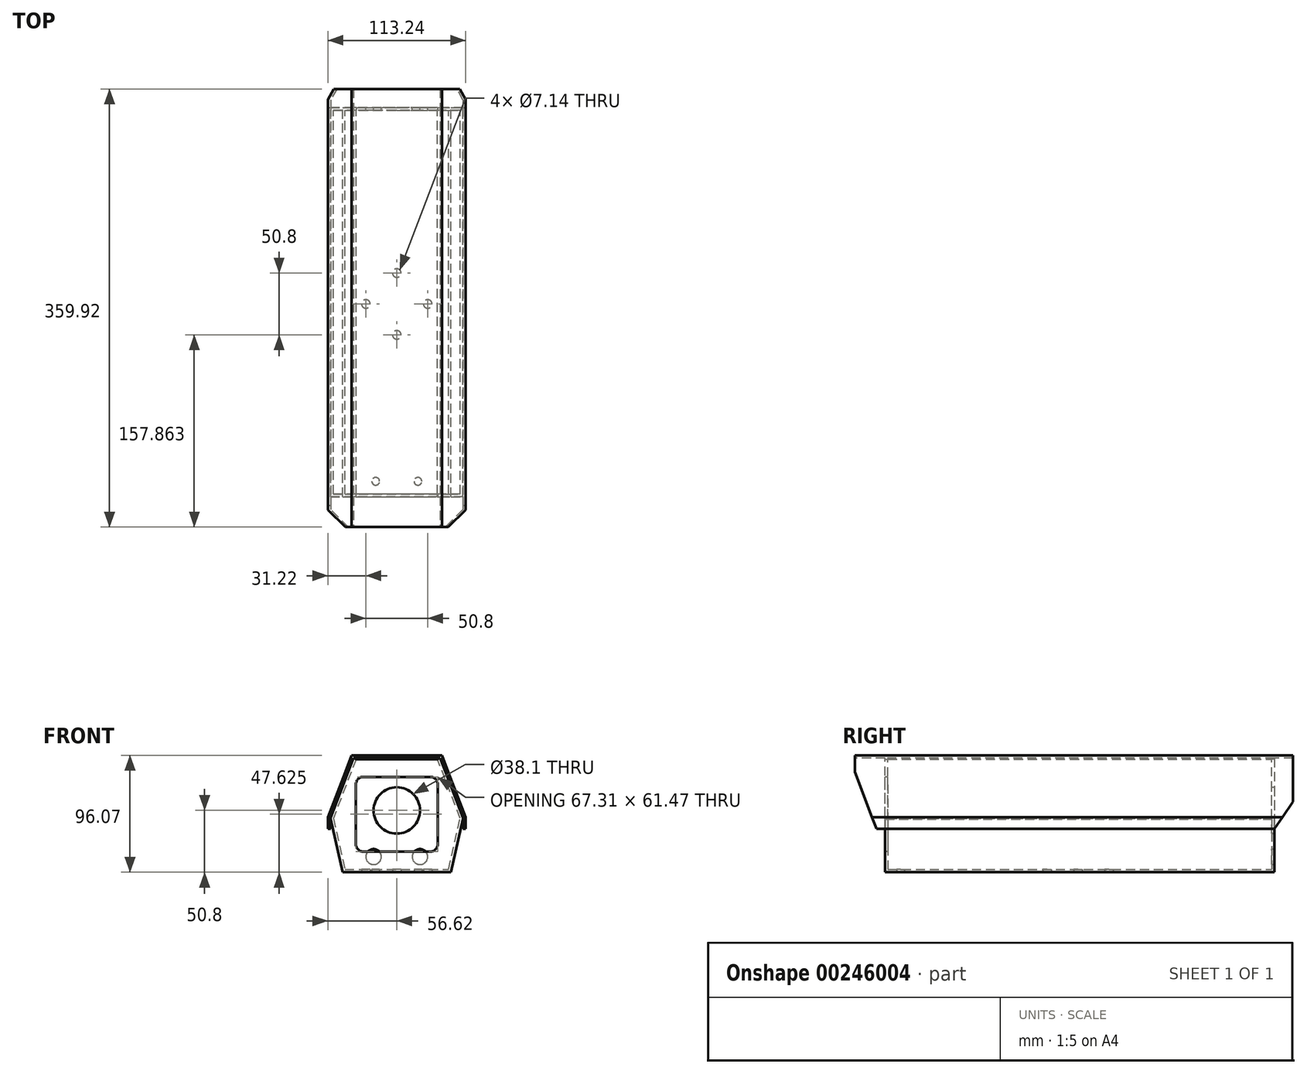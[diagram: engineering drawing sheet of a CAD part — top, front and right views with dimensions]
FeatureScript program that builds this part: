
annotation { "Feature Type Name" : "Feature", "Feature Type Description" : "" }
export const myFeature = defineFeature(function(context is Context, id is Id, definition is map)
    precondition{}
    {
        {
            var Q0;
            Q0=qCreatedBy(makeId("Front.planeOp"),FACE);
            var sketch = newSketch(context, id + "F0", { "sketchPlane" : qUnion([Q0])});
            skLineSegment(sketch, "E0", {"start": v(-44.45, 0) * mm, "end": v(44.45, 0) * mm});
            skLineSegment(sketch, "E1", {"start": v(44.45, 0) * mm, "end": v(54.48, 44.45) * mm});
            skLineSegment(sketch, "E2", {"start": v(54.48, 44.45) * mm, "end": v(34.92, 95.25) * mm});
            skLineSegment(sketch, "E3", {"start": v(34.92, 95.25) * mm, "end": v(-34.92, 95.25) * mm});
            skLineSegment(sketch, "E4", {"start": v(-34.92, 95.25) * mm, "end": v(-54.48, 44.45) * mm});
            skLineSegment(sketch, "E5", {"start": v(-54.48, 44.45) * mm, "end": v(-44.45, 0) * mm});
            skLineSegment(sketch, "E6", {"start": v(0, -51.88) * mm, "end": v(0, 117.86) * mm, "construction": true});
            skSolve(sketch);
        }
        {
            var Q0;
            Q0=makeQuery(id+"F0.imprint","IMPRINT",FACE,{"disambiguationData":[TD([[makeQuery(id+"F0.imprint","IMPRINT",EDGE,{"derivedFrom":sQuery(id+"F0.wireOp",EDGE,"E0")}),1.0]])]});
            extrude(context, id + "F1", {"entities" : qUnion([Q0]), "depth" : 319.8 * mm});
        }
        {
            var Q0;
            Q0=makeQuery(id+"F1.opExtrude","CAP_FACE",FACE,{"disambiguationData":[OSD([sQuery(id+"F0.wireOp",EDGE,"E0"),sQuery(id+"F0.wireOp",EDGE,"E1"),sQuery(id+"F0.wireOp",EDGE,"E2"),sQuery(id+"F0.wireOp",EDGE,"E3"),sQuery(id+"F0.wireOp",EDGE,"E4"),sQuery(id+"F0.wireOp",EDGE,"E5")])],"isStart":false});
            shell(context, id + "F2", {"entities" : qUnion([Q0]), "thickness" : 2.3 * mm});
        }
        {
            var Q0;
            Q0=makeQuery(id+"F1.opExtrude","CAP_FACE",FACE,{"disambiguationData":[OSD([sQuery(id+"F0.wireOp",EDGE,"E0"),sQuery(id+"F0.wireOp",EDGE,"E1"),sQuery(id+"F0.wireOp",EDGE,"E2"),sQuery(id+"F0.wireOp",EDGE,"E3"),sQuery(id+"F0.wireOp",EDGE,"E4"),sQuery(id+"F0.wireOp",EDGE,"E5")])],"isStart":true});
            var sketch = newSketch(context, id + "F3", { "sketchPlane" : qUnion([Q0])});
            skCircle(sketch, "E7", {"center": v(-19.05, 12.7) * mm, "radius": 6.35 * mm});
            skCircle(sketch, "E8", {"center": v(19.05, 12.7) * mm, "radius": 6.35 * mm});
            skLineSegment(sketch, "E9", {"start": v(0, 105.87) * mm, "end": v(0, -20.53) * mm, "construction": true});
            skSolve(sketch);
        }
        {
            var Q0;
            Q0=makeQuery(id+"F3.imprint","IMPRINT",FACE,{"disambiguationData":[TD([[makeQuery(id+"F3.imprint","IMPRINT",EDGE,{"derivedFrom":sQuery(id+"F3.wireOp",EDGE,"E7")}),1.0]])]});
            var Q1;
            Q1=makeQuery(id+"F3.imprint","IMPRINT",FACE,{"disambiguationData":[TD([[makeQuery(id+"F3.imprint","IMPRINT",EDGE,{"derivedFrom":sQuery(id+"F3.wireOp",EDGE,"E8")}),1.0]])]});
            extrude(context, id + "F4", {"entities" : qUnion([Q0, Q1]), "operationType" : NewBodyOperationType.REMOVE, "endBound" : BoundingType.UP_TO_NEXT, "oppositeDirection" : true, "depth" : 25.4 * mm});
        }
        {
            var Q0;
            Q0=makeQuery(id+"F1.opExtrude","CAP_FACE",FACE,{"disambiguationData":[OSD([sQuery(id+"F0.wireOp",EDGE,"E0"),sQuery(id+"F0.wireOp",EDGE,"E1"),sQuery(id+"F0.wireOp",EDGE,"E2"),sQuery(id+"F0.wireOp",EDGE,"E3"),sQuery(id+"F0.wireOp",EDGE,"E4"),sQuery(id+"F0.wireOp",EDGE,"E5")])],"isStart":true});
            var sketch = newSketch(context, id + "F5", { "sketchPlane" : qUnion([Q0])});
            skCircle(sketch, "E10", {"center": v(0, 50.8) * mm, "radius": 19.05 * mm});
            skSolve(sketch);
        }
        {
            var Q0;
            Q0=makeQuery(id+"F5.imprint","IMPRINT",FACE,{"disambiguationData":[TD([[makeQuery(id+"F5.imprint","IMPRINT",EDGE,{"derivedFrom":sQuery(id+"F5.wireOp",EDGE,"E10")}),1.0]])]});
            extrude(context, id + "F6", {"entities" : qUnion([Q0]), "operationType" : NewBodyOperationType.REMOVE, "endBound" : BoundingType.UP_TO_NEXT, "oppositeDirection" : true, "depth" : 25.4 * mm});
        }
        {
            var Q0;
            Q0=makeQuery(id+"F1.opExtrude","SWEPT_FACE",FACE,{"disambiguationData":[OSD([sQuery(id+"F0.wireOp",EDGE,"E0")])]});
            var sketch = newSketch(context, id + "F7", { "sketchPlane" : qUnion([Q0])});
            skPoint(sketch, "E11", {"position": v(17.33, 307.09) * mm});
            skPoint(sketch, "E11.positionSnap0", {"position": v(0, 319.79) * mm});
            skPoint(sketch, "E12", {"position": v(-17.33, 307.09) * mm});
            skSolve(sketch);
        }
        {
            var Q0;
            Q0=sQuery(id+"F7.wireOp",VERTEX,"E11");
            var Q1;
            Q1=sQuery(id+"F7.wireOp",VERTEX,"E12");
            var Q2;
            Q2=makeQuery(id+"F1.opExtrude","SWEPT_BODY",BODY,{"disambiguationData":[OSD([sQuery(id+"F0.wireOp",EDGE,"E0"),sQuery(id+"F0.wireOp",EDGE,"E1"),sQuery(id+"F0.wireOp",EDGE,"E2"),sQuery(id+"F0.wireOp",EDGE,"E3"),sQuery(id+"F0.wireOp",EDGE,"E4"),sQuery(id+"F0.wireOp",EDGE,"E5")])]});
            hole(context, id + "F8", {"style" : HoleStyle.SIMPLE, "endStyle" : HoleEndStyle.BLIND, "holeDiameter" : 6.35 * mm, "holeDepth" : 12.7 * mm, "tappedDepth" : 12.7 * mm, "tapClearance" : 3, "locations" : qUnion([Q0, Q1]), "scope" : qUnion([Q2])});
        }
        {
            var Q0;
            Q0=makeQuery(id+"F1.opExtrude","CAP_FACE",FACE,{"disambiguationData":[OSD([sQuery(id+"F0.wireOp",EDGE,"E0"),sQuery(id+"F0.wireOp",EDGE,"E1"),sQuery(id+"F0.wireOp",EDGE,"E2"),sQuery(id+"F0.wireOp",EDGE,"E3"),sQuery(id+"F0.wireOp",EDGE,"E4"),sQuery(id+"F0.wireOp",EDGE,"E5")])],"isStart":false});
            var sketch = newSketch(context, id + "F9", { "sketchPlane" : qUnion([Q0])});
            skLineSegment(sketch, "E13", {"start": v(-33.36, 92.96) * mm, "end": v(-44.54, 97.27) * mm});
            skLineSegment(sketch, "E14", {"start": v(-44.54, 97.27) * mm, "end": v(-44.54, 106.46) * mm});
            skLineSegment(sketch, "E15", {"start": v(-44.54, 106.46) * mm, "end": v(45.86, 106.46) * mm});
            skLineSegment(sketch, "E16", {"start": v(33.36, 92.96) * mm, "end": v(45.86, 97.78) * mm});
            skLineSegment(sketch, "E17", {"start": v(45.86, 106.46) * mm, "end": v(45.86, 97.78) * mm});
            skLineSegment(sketch, "E18", {"start": v(-33.36, 92.96) * mm, "end": v(33.36, 92.96) * mm});
            skSolve(sketch);
        }
        {
            var Q0;
            {var subQ0=sQuery(id+"F9.wireOp",EDGE,"E14");Q0=makeQuery(id+"F9.imprint","IMPRINT",FACE,{"disambiguationData":[TD([[makeQuery(id+"F9.imprint","IMPRINT",EDGE,{"derivedFrom":subQ0}),-1.0]])]});}
            var Q1;
            {var subQ0=sQuery(id+"F9.wireOp",EDGE,"E18");Q1=makeQuery(id+"F9.imprint","IMPRINT",FACE,{"disambiguationData":[TD([[makeQuery(id+"F9.imprint","IMPRINT",EDGE,{"derivedFrom":subQ0}),-1.0]])]});}
            extrude(context, id + "F10", {"entities" : qUnion([Q0, Q1]), "operationType" : NewBodyOperationType.REMOVE, "endBound" : BoundingType.THROUGH_ALL, "oppositeDirection" : true, "depth" : 25.4 * mm});
        }
        {
            var Q0;
            {var subQ0=sQuery(id+"F9.wireOp",EDGE,"E14");Q0=makeQuery(id+"F9.imprint","IMPRINT",FACE,{"disambiguationData":[TD([[makeQuery(id+"F9.imprint","IMPRINT",EDGE,{"derivedFrom":subQ0}),-1.0]])]});}
            var Q1;
            {var subQ0=sQuery(id+"F9.wireOp",EDGE,"E18");Q1=makeQuery(id+"F9.imprint","IMPRINT",FACE,{"disambiguationData":[TD([[makeQuery(id+"F9.imprint","IMPRINT",EDGE,{"derivedFrom":subQ0}),-1.0]])]});}
            extrude(context, id + "F11", {"entities" : qUnion([Q0, Q1]), "operationType" : NewBodyOperationType.REMOVE, "endBound" : BoundingType.THROUGH_ALL, "oppositeDirection" : true, "depth" : 25.4 * mm});
        }
        {
            var Q0;
            Q0=makeQuery(id+"F1.opExtrude","CAP_FACE",FACE,{"disambiguationData":[OSD([sQuery(id+"F0.wireOp",EDGE,"E0"),sQuery(id+"F0.wireOp",EDGE,"E1"),sQuery(id+"F0.wireOp",EDGE,"E2"),sQuery(id+"F0.wireOp",EDGE,"E3"),sQuery(id+"F0.wireOp",EDGE,"E4"),sQuery(id+"F0.wireOp",EDGE,"E5")])],"isStart":false});
            var sketch = newSketch(context, id + "F12", { "sketchPlane" : qUnion([Q0])});
            skLineSegment(sketch, "E19", {"start": v(-33.36, 92.96) * mm, "end": v(-52.1, 44.28) * mm});
            skLineSegment(sketch, "E20", {"start": v(-52.1, 44.28) * mm, "end": v(-42.62, 2.29) * mm});
            skLineSegment(sketch, "E21", {"start": v(-42.62, 2.29) * mm, "end": v(42.62, 2.29) * mm});
            skLineSegment(sketch, "E22", {"start": v(42.62, 2.29) * mm, "end": v(52.1, 44.28) * mm});
            skLineSegment(sketch, "E23", {"start": v(52.1, 44.28) * mm, "end": v(33.36, 92.96) * mm});
            skLineSegment(sketch, "E24", {"start": v(33.36, 92.96) * mm, "end": v(-33.36, 92.96) * mm});
            skSolve(sketch);
        }
        {
            var Q0;
            Q0=makeQuery(id+"F12.imprint","IMPRINT",FACE,{"disambiguationData":[TD([[makeQuery(id+"F12.imprint","IMPRINT",EDGE,{"derivedFrom":sQuery(id+"F12.wireOp",EDGE,"E19")}),1.0]])]});
            extrude(context, id + "F13", {"entities" : qUnion([Q0]), "operationType" : NewBodyOperationType.ADD, "oppositeDirection" : true, "depth" : 2.3 * mm});
        }
        {
            var Q0;
            Q0=makeQuery(id+"F13.opExtrude","CAP_FACE",FACE,{"disambiguationData":[OSD([sQuery(id+"F12.wireOp",EDGE,"E19"),sQuery(id+"F12.wireOp",EDGE,"E20"),sQuery(id+"F12.wireOp",EDGE,"E21"),sQuery(id+"F12.wireOp",EDGE,"E22"),sQuery(id+"F12.wireOp",EDGE,"E23"),sQuery(id+"F12.wireOp",EDGE,"E24")])],"isStart":true});
            var sketch = newSketch(context, id + "F14", { "sketchPlane" : qUnion([Q0])});
            skLineSegment(sketch, "E25.bottom", {"start": v(-27.3, 16.9) * mm, "end": v(27.3, 16.9) * mm});
            skLineSegment(sketch, "E25.top", {"start": v(-27.3, 78.36) * mm, "end": v(27.3, 78.36) * mm});
            skLineSegment(sketch, "E25.left", {"start": v(-33.65, 23.24) * mm, "end": v(-33.66, 72) * mm});
            skLineSegment(sketch, "E25.right", {"start": v(33.66, 23.24) * mm, "end": v(33.66, 72) * mm});
            skPoint(sketch, "E26.visualSharp", {"position": v(-33.66, 78.36) * mm});
            skArc(sketch, "E26.filletArc", {"start": v(-27.3, 78.36) * mm, "mid": v(-31.8, 76.5) * mm, "end": v(-33.66, 72) * mm});
            skPoint(sketch, "E27.visualSharp", {"position": v(33.66, 78.36) * mm});
            skArc(sketch, "E27.filletArc", {"start": v(33.66, 72) * mm, "mid": v(31.8, 76.5) * mm, "end": v(27.3, 78.36) * mm});
            skPoint(sketch, "E28.visualSharp", {"position": v(33.66, 16.9) * mm});
            skArc(sketch, "E28.filletArc", {"start": v(27.3, 16.9) * mm, "mid": v(31.8, 18.75) * mm, "end": v(33.66, 23.24) * mm});
            skPoint(sketch, "E29.visualSharp", {"position": v(-33.65, 16.9) * mm});
            skArc(sketch, "E29.filletArc", {"start": v(-33.66, 23.24) * mm, "mid": v(-31.8, 18.75) * mm, "end": v(-27.3, 16.9) * mm});
            skLineSegment(sketch, "E30", {"start": v(0, 92.96) * mm, "end": v(0, 2.29) * mm, "construction": true});
            skPoint(sketch, "E30.startSnap0", {"position": v(0, 92.96) * mm});
            skPoint(sketch, "E30.endSnap0", {"position": v(0, 2.29) * mm});
            skPoint(sketch, "E31.orphan", {"position": v(0, 104.06) * mm});
            skPoint(sketch, "E32.orphan", {"position": v(0, -5.79) * mm});
            skLineSegment(sketch, "E33", {"start": v(-68.53, 47.63) * mm, "end": v(65.13, 47.63) * mm, "construction": true});
            skPoint(sketch, "E33.startSnap0", {"position": v(0, 47.63) * mm});
            skSolve(sketch);
        }
        {
            var Q0;
            Q0=makeQuery(id+"F14.imprint","IMPRINT",FACE,{"disambiguationData":[TD([[makeQuery(id+"F14.imprint","IMPRINT",EDGE,{"derivedFrom":sQuery(id+"F14.wireOp",EDGE,"E25.bottom")}),1.0]])]});
            extrude(context, id + "F15", {"entities" : qUnion([Q0]), "operationType" : NewBodyOperationType.REMOVE, "endBound" : BoundingType.UP_TO_NEXT, "oppositeDirection" : true, "depth" : 25.4 * mm});
        }
        {
            var Q0;
            Q0=makeQuery(id+"F13.opExtrude","CAP_FACE",FACE,{"disambiguationData":[OSD([sQuery(id+"F12.wireOp",EDGE,"E19"),sQuery(id+"F12.wireOp",EDGE,"E20"),sQuery(id+"F12.wireOp",EDGE,"E21"),sQuery(id+"F12.wireOp",EDGE,"E22"),sQuery(id+"F12.wireOp",EDGE,"E23"),sQuery(id+"F12.wireOp",EDGE,"E24")])],"isStart":true});
            cPlane(context, id + "F16", {"entities" : qUnion([Q0]), "cplaneType" : CPlaneType.OFFSET, "offset" : 24.9 * mm, "width" : 152.4 * mm, "height" : 152.4 * mm});
        }
        {
            var Q0;
            Q0=qCreatedBy(id+"F16.planeOp",FACE);
            var sketch = newSketch(context, id + "F17", { "sketchPlane" : qUnion([Q0])});
            skLineSegment(sketch, "E34.0", {"start": v(-37.06, 96.07) * mm, "end": v(-56.62, 45.27) * mm});
            skLineSegment(sketch, "E35.0", {"start": v(56.62, 45.27) * mm, "end": v(37.06, 96.07) * mm});
            skLineSegment(sketch, "E36", {"start": v(-56.62, 45.27) * mm, "end": v(-56.62, 35.75) * mm});
            skLineSegment(sketch, "E37", {"start": v(56.62, 45.27) * mm, "end": v(56.62, 35.75) * mm});
            skLineSegment(sketch, "E38", {"start": v(-56.62, 35.75) * mm, "end": v(-54.33, 35.75) * mm});
            skLineSegment(sketch, "E39", {"start": v(56.62, 35.75) * mm, "end": v(54.33, 35.75) * mm});
            skLineSegment(sketch, "E40", {"start": v(54.33, 35.75) * mm, "end": v(54.33, 44.85) * mm});
            skLineSegment(sketch, "E41.0", {"start": v(54.33, 44.85) * mm, "end": v(35.49, 93.79) * mm});
            skPoint(sketch, "E42.orphan", {"position": v(54.48, 44.45) * mm});
            skLineSegment(sketch, "E43.0", {"start": v(-35.49, 93.79) * mm, "end": v(-54.33, 44.85) * mm});
            skLineSegment(sketch, "E44", {"start": v(-35.49, 93.79) * mm, "end": v(35.49, 93.79) * mm});
            skLineSegment(sketch, "E45.0", {"start": v(-37.06, 96.07) * mm, "end": v(37.06, 96.07) * mm});
            skPoint(sketch, "E46.orphan", {"position": v(-43.27, 93.79) * mm});
            skLineSegment(sketch, "E47", {"start": v(-54.33, 35.75) * mm, "end": v(-54.33, 44.85) * mm});
            skPoint(sketch, "E48.orphan", {"position": v(-54.48, 44.45) * mm});
            skSolve(sketch);
        }
        {
            var Q0;
            Q0=makeQuery(id+"F17.imprint","IMPRINT",FACE,{"disambiguationData":[TD([[makeQuery(id+"F17.imprint","IMPRINT",EDGE,{"derivedFrom":sQuery(id+"F17.wireOp",EDGE,"E34.0")}),1.0]])]});
            extrude(context, id + "F18", {"entities" : qUnion([Q0]), "operationType" : NewBodyOperationType.ADD, "oppositeDirection" : true, "depth" : 359.92 * mm});
        }
        {
            var Q0;
            Q0=makeQuery(id+"F18.opExtrude","SWEPT_FACE",FACE,{"disambiguationData":[OSD([sQuery(id+"F17.wireOp",EDGE,"E37")])]});
            var sketch = newSketch(context, id + "F19", { "sketchPlane" : qUnion([Q0])});
            skLineSegment(sketch, "E49", {"start": v(-326.87, 35.75) * mm, "end": v(-344.68, 82.46) * mm});
            skLineSegment(sketch, "E50.0", {"start": v(-344.68, 35.75) * mm, "end": v(-344.68, 82.46) * mm});
            skLineSegment(sketch, "E51.0", {"start": v(-326.87, 35.75) * mm, "end": v(-344.68, 35.75) * mm});
            skPoint(sketch, "E52.orphan", {"position": v(15.24, 35.75) * mm});
            skPoint(sketch, "E53.orphan", {"position": v(-344.68, 45.27) * mm});
            skPoint(sketch, "E54.orphan", {"position": v(-344.68, 96.07) * mm});
            skSolve(sketch);
        }
        {
            var Q0;
            {var subQ0=sQuery(id+"F19.wireOp",EDGE,"E50.0");var subQ1=sQuery(id+"F19.wireOp",EDGE,"E49");var subQ2=makeQuery(id+"F19.imprint","INTERSECT",VERTEX,{"derivedFrom":[subQ1,subQ0]});Q0=makeQuery(id+"F19.imprint","IMPRINT",FACE,{"disambiguationData":[TD([[makeQuery(id+"F19.imprint","IMPRINT",EDGE,{"disambiguationData":[TD([[subQ2,1.0]])],"derivedFrom":subQ1}),1.0]])]});}
            var Q1;
            {var subQ0=sQuery(id+"F19.wireOp",EDGE,"E51.0");Q1=makeQuery(id+"F19.imprint","IMPRINT",FACE,{"disambiguationData":[TD([[makeQuery(id+"F19.imprint","IMPRINT",EDGE,{"derivedFrom":subQ0}),-1.0]])]});}
            extrude(context, id + "F20", {"entities" : qUnion([Q0, Q1]), "operationType" : NewBodyOperationType.REMOVE, "endBound" : BoundingType.THROUGH_ALL, "oppositeDirection" : true, "depth" : 25.4 * mm});
        }
        {
            var Q0;
            Q0=makeQuery(id+"F18.opExtrude","SWEPT_FACE",FACE,{"disambiguationData":[OSD([sQuery(id+"F17.wireOp",EDGE,"E37")])]});
            var sketch = newSketch(context, id + "F21", { "sketchPlane" : qUnion([Q0])});
            skLineSegment(sketch, "E55", {"start": v(0, 35.75) * mm, "end": v(15.24, 57.8) * mm});
            skLineSegment(sketch, "E56.0", {"start": v(15.24, 35.75) * mm, "end": v(15.24, 57.8) * mm});
            skLineSegment(sketch, "E57.0", {"start": v(15.24, 35.75) * mm, "end": v(0, 35.75) * mm});
            skPoint(sketch, "E58.orphan", {"position": v(-326.87, 35.75) * mm});
            skPoint(sketch, "E59.orphan", {"position": v(15.24, 96.07) * mm});
            skPoint(sketch, "E60.orphan", {"position": v(15.24, 45.27) * mm});
            skSolve(sketch);
        }
        {
            var Q0;
            {var subQ0=sQuery(id+"F21.wireOp",EDGE,"E56.0");var subQ1=sQuery(id+"F21.wireOp",EDGE,"E55");var subQ2=makeQuery(id+"F21.imprint","INTERSECT",VERTEX,{"derivedFrom":[subQ1,subQ0]});Q0=makeQuery(id+"F21.imprint","IMPRINT",FACE,{"disambiguationData":[TD([[makeQuery(id+"F21.imprint","IMPRINT",EDGE,{"disambiguationData":[TD([[subQ2,1.0]])],"derivedFrom":subQ1}),-1.0]])]});}
            var Q1;
            {var subQ0=sQuery(id+"F21.wireOp",EDGE,"E57.0");Q1=makeQuery(id+"F21.imprint","IMPRINT",FACE,{"disambiguationData":[TD([[makeQuery(id+"F21.imprint","IMPRINT",EDGE,{"derivedFrom":subQ0}),-1.0]])]});}
            extrude(context, id + "F22", {"entities" : qUnion([Q0, Q1]), "operationType" : NewBodyOperationType.REMOVE, "endBound" : BoundingType.THROUGH_ALL, "oppositeDirection" : true, "depth" : 25.4 * mm});
        }
        {
            var Q0;
            {var subQ0=sQuery(id+"F21.wireOp",EDGE,"E56.0");var subQ1=sQuery(id+"F21.wireOp",EDGE,"E55");var subQ2=makeQuery(id+"F21.imprint","INTERSECT",VERTEX,{"derivedFrom":[subQ1,subQ0]});Q0=makeQuery(id+"F21.imprint","IMPRINT",FACE,{"disambiguationData":[TD([[makeQuery(id+"F21.imprint","IMPRINT",EDGE,{"disambiguationData":[TD([[subQ2,1.0]])],"derivedFrom":subQ1}),-1.0]])]});}
            var Q1;
            {var subQ0=sQuery(id+"F21.wireOp",EDGE,"E57.0");Q1=makeQuery(id+"F21.imprint","IMPRINT",FACE,{"disambiguationData":[TD([[makeQuery(id+"F21.imprint","IMPRINT",EDGE,{"derivedFrom":subQ0}),-1.0]])]});}
            extrude(context, id + "F23", {"entities" : qUnion([Q0, Q1]), "operationType" : NewBodyOperationType.REMOVE, "endBound" : BoundingType.THROUGH_ALL, "oppositeDirection" : true, "depth" : 25.4 * mm});
        }
        {
            var Q0;
            Q0=makeQuery(id+"F1.opExtrude","SWEPT_FACE",FACE,{"disambiguationData":[OSD([sQuery(id+"F0.wireOp",EDGE,"E0")])]});
            var sketch = newSketch(context, id + "F24", { "sketchPlane" : qUnion([Q0])});
            skPoint(sketch, "E61", {"position": v(0, 136.02) * mm});
            skPoint(sketch, "E62", {"position": v(0, 186.82) * mm});
            skPoint(sketch, "E63", {"position": v(25.4, 161.42) * mm});
            skPoint(sketch, "E64", {"position": v(-25.4, 161.42) * mm});
            skSolve(sketch);
        }
        {
            var Q0;
            Q0=sQuery(id+"F24.wireOp",VERTEX,"9292a717-25cd-4ec0-970a-25e66ca9a175");
            var Q1;
            Q1=sQuery(id+"F24.wireOp",VERTEX,"E63");
            var Q2;
            Q2=sQuery(id+"F24.wireOp",VERTEX,"41b86ec4-f55c-46c5-a506-1770a1f02db4");
            var Q3;
            Q3=sQuery(id+"F24.wireOp",VERTEX,"E61");
            var Q4;
            Q4=sQuery(id+"F24.wireOp",VERTEX,"d50fe409-6bdb-475d-af91-d32197417cb6");
            var Q5;
            Q5=sQuery(id+"F24.wireOp",VERTEX,"E62");
            var Q6;
            Q6=sQuery(id+"F24.wireOp",VERTEX,"E64");
            var Q7;
            Q7=makeQuery(id+"F1.opExtrude","SWEPT_BODY",BODY,{"disambiguationData":[OSD([sQuery(id+"F0.wireOp",EDGE,"E0"),sQuery(id+"F0.wireOp",EDGE,"E1"),sQuery(id+"F0.wireOp",EDGE,"E2"),sQuery(id+"F0.wireOp",EDGE,"E3"),sQuery(id+"F0.wireOp",EDGE,"E4"),sQuery(id+"F0.wireOp",EDGE,"E5")])]});
            hole(context, id + "F25", {"style" : HoleStyle.SIMPLE, "endStyle" : HoleEndStyle.BLIND, "holeDiameter" : 7.14 * mm, "holeDepth" : 6.35 * mm, "tappedDepth" : 12.7 * mm, "tapClearance" : 3, "locations" : qUnion([Q0, Q1, Q2, Q3, Q4, Q5, Q6]), "scope" : qUnion([Q7])});
        }
    });
